# Revit family: DA-195_CH
name_source: partatom
category: Plumbing Fixtures
revit_build: Autodesk Revit Architecture 2012 (Build: 20110309_2315(x64)
units: mm (PartAtom-declared; Revit-internal decimal feet)

## types (1)
- DA-195/CH
    Aerator = C-M22X1-FLEX
    Angle regulating valve = 232-10
    Assembly Code = D2010
    CW Connection = Yes
    CWFU = 0
    Chain = 090
    Connection tubes = C-M10X1/2
    Cost = 0 $
    Default Elevation = 0' - 0"
    Description = One hole + swivel outlet + waste + plug + chain. Angle valves. 1/4 turn. 1/2"FI
    HW Connection = Yes
    HWFU = 0
    Headpart anti-clockwise closing = S-21-2ANTI
    Headpart clockwise closing = S-21-1CLOCK
    Keynote = 2 x 1/2" female iron 400mm long flexible inlets
    Manufacturer = COBRA
    Material = Chrome - Polished
    Model = DA-195/CH
    Range = Damara
    Slotted waste = 301
    Type Comments = SANS 226 TYPE 2
    Vent Connection = No
    WFU = 0
    Waste Connection = Yes

## geometry (parser evidence)
native form markers: Blend x2
no freeform markers — native parametric forms only
